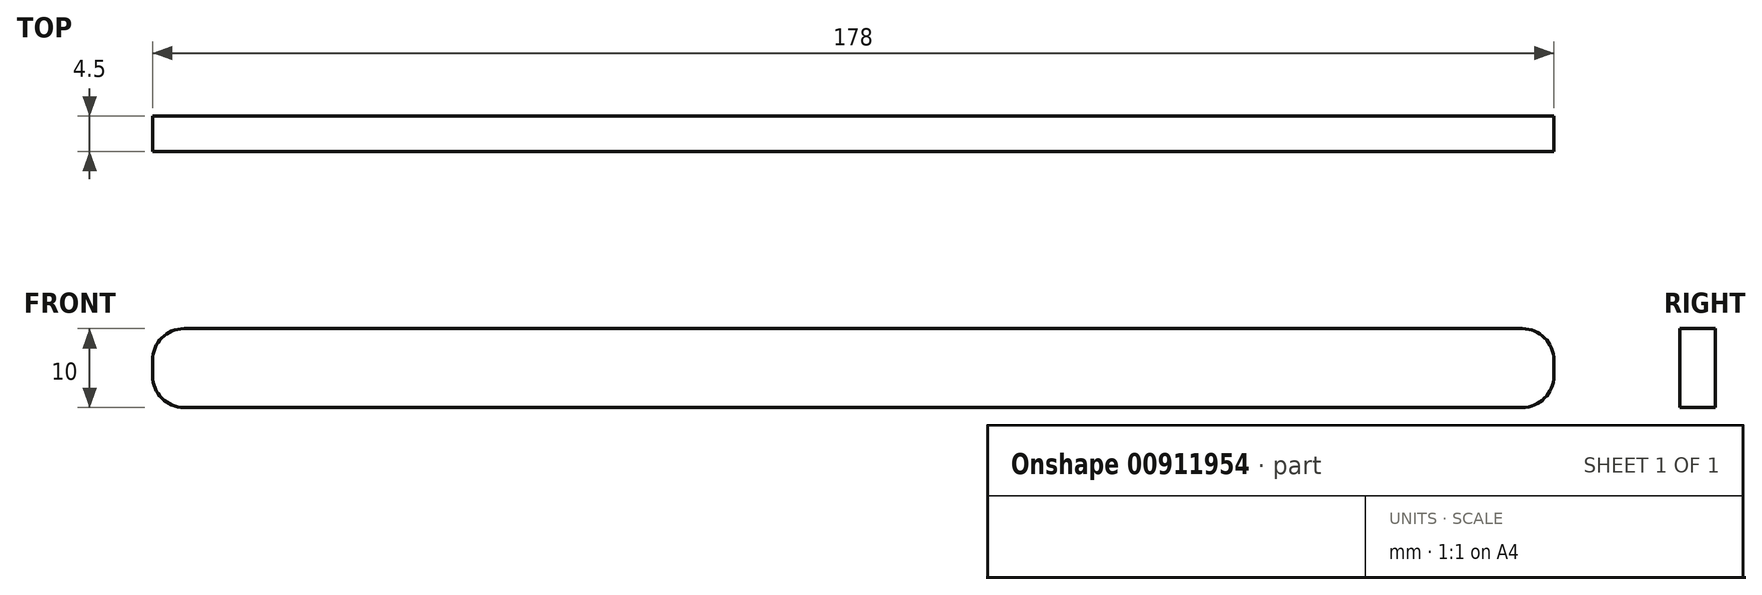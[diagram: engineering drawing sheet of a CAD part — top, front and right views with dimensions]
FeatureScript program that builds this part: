
annotation { "Feature Type Name" : "Feature", "Feature Type Description" : "" }
export const myFeature = defineFeature(function(context is Context, id is Id, definition is map)
    precondition{}
    {
        {
            var Q0;
            Q0=qCreatedBy(makeId("Front.planeOp"),FACE);
            var sketch = newSketch(context, id + "F0", { "sketchPlane" : qUnion([Q0])});
            skLineSegment(sketch, "E0.bottom", {"start": v(-29.45, 22.82) * mm, "end": v(140.55, 22.82) * mm});
            skLineSegment(sketch, "E0.top", {"start": v(-29.45, 12.82) * mm, "end": v(140.55, 12.82) * mm});
            skLineSegment(sketch, "E0.left", {"start": v(-33.45, 18.82) * mm, "end": v(-33.45, 16.82) * mm});
            skLineSegment(sketch, "E0.right", {"start": v(144.55, 18.82) * mm, "end": v(144.55, 16.82) * mm});
            skPoint(sketch, "E1.visualSharp", {"position": v(-33.45, 22.82) * mm});
            skArc(sketch, "E1.filletArc", {"start": v(-29.45, 22.82) * mm, "mid": v(-32.28, 21.64) * mm, "end": v(-33.45, 18.82) * mm});
            skPoint(sketch, "E2.visualSharp", {"position": v(-33.45, 12.82) * mm});
            skArc(sketch, "E2.filletArc", {"start": v(-33.45, 16.82) * mm, "mid": v(-32.28, 13.99) * mm, "end": v(-29.45, 12.82) * mm});
            skPoint(sketch, "E3.visualSharp", {"position": v(144.55, 22.82) * mm});
            skArc(sketch, "E3.filletArc", {"start": v(144.55, 18.82) * mm, "mid": v(143.38, 21.64) * mm, "end": v(140.55, 22.82) * mm});
            skPoint(sketch, "E4.visualSharp", {"position": v(144.55, 12.82) * mm});
            skArc(sketch, "E4.filletArc", {"start": v(140.55, 12.82) * mm, "mid": v(143.38, 13.99) * mm, "end": v(144.55, 16.82) * mm});
            skSolve(sketch);
        }
        {
            var Q0;
            Q0=makeQuery(id+"F0.imprint","IMPRINT",FACE,{"disambiguationData":[TD([[makeQuery(id+"F0.imprint","IMPRINT",EDGE,{"derivedFrom":sQuery(id+"F0.wireOp",EDGE,"E0.bottom")}),-1.0]])]});
            var Q1;
            Q1=makeQuery(id+"F0.imprint","IMPRINT",FACE,{"disambiguationData":[TD([[makeQuery(id+"F0.imprint","IMPRINT",EDGE,{"derivedFrom":sQuery(id+"F0.wireOp",EDGE,"70d934ce-e17f-45e3-ae2d-8f623205eb24.bottom")}),-1.0]])]});
            extrude(context, id + "F1", {"entities" : qUnion([Q0, Q1]), "depth" : 4.5 * mm, "offsetDistance" : 25 * mm});
        }
    });
